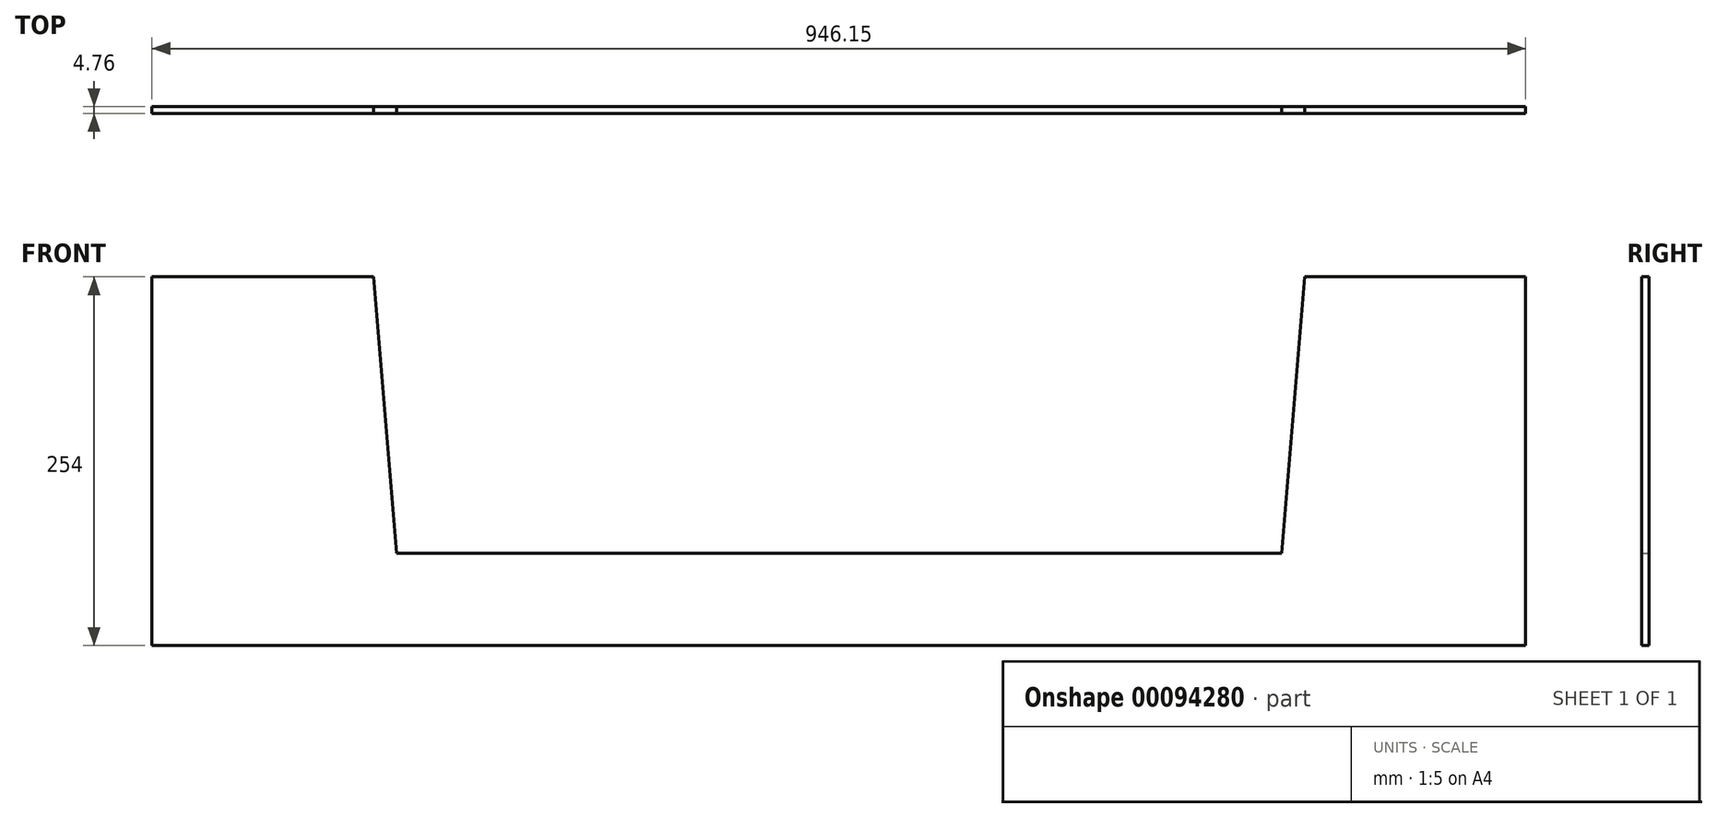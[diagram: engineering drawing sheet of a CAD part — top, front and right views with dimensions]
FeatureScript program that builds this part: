
annotation { "Feature Type Name" : "Feature", "Feature Type Description" : "" }
export const myFeature = defineFeature(function(context is Context, id is Id, definition is map)
    precondition{}
    {
        {
            var Q0;
            Q0=qCreatedBy(makeId("Front.planeOp"),FACE);
            var sketch = newSketch(context, id + "F0", { "sketchPlane" : qUnion([Q0])});
            skLineSegment(sketch, "E0.top", {"start": v(486.51, -127) * mm, "end": v(-459.64, -127) * mm});
            skLineSegment(sketch, "E0.left", {"start": v(486.51, 127) * mm, "end": v(486.51, -127) * mm});
            skLineSegment(sketch, "E0.right", {"start": v(-459.64, 127) * mm, "end": v(-459.64, -127) * mm});
            skPoint(sketch, "E0.middle", {"position": v(13.44, 0) * mm});
            skLineSegment(sketch, "E1.top", {"start": v(-291.36, -63.5) * mm, "end": v(318.24, -63.5) * mm});
            skLineSegment(sketch, "E2.trimOffspring", {"start": v(-307.24, 127) * mm, "end": v(-459.64, 127) * mm});
            skLineSegment(sketch, "E3", {"start": v(486.51, 127) * mm, "end": v(334.11, 127) * mm});
            skLineSegment(sketch, "E4", {"start": v(-291.36, -63.5) * mm, "end": v(-307.24, 127) * mm});
            skLineSegment(sketch, "E5", {"start": v(318.24, -63.5) * mm, "end": v(334.11, 127) * mm});
            skPoint(sketch, "E6.orphan", {"position": v(-367.8, 127) * mm});
            skPoint(sketch, "E1.right.start.orphan", {"position": v(394.44, 127) * mm});
            skSolve(sketch);
        }
        {
            var Q0;
            Q0 = qSketchRegion(id + "F0", true);
            extrude(context, id + "F1", {"entities" : qUnion([Q0]), "depth" : 4.76 * mm});
        }
    });
